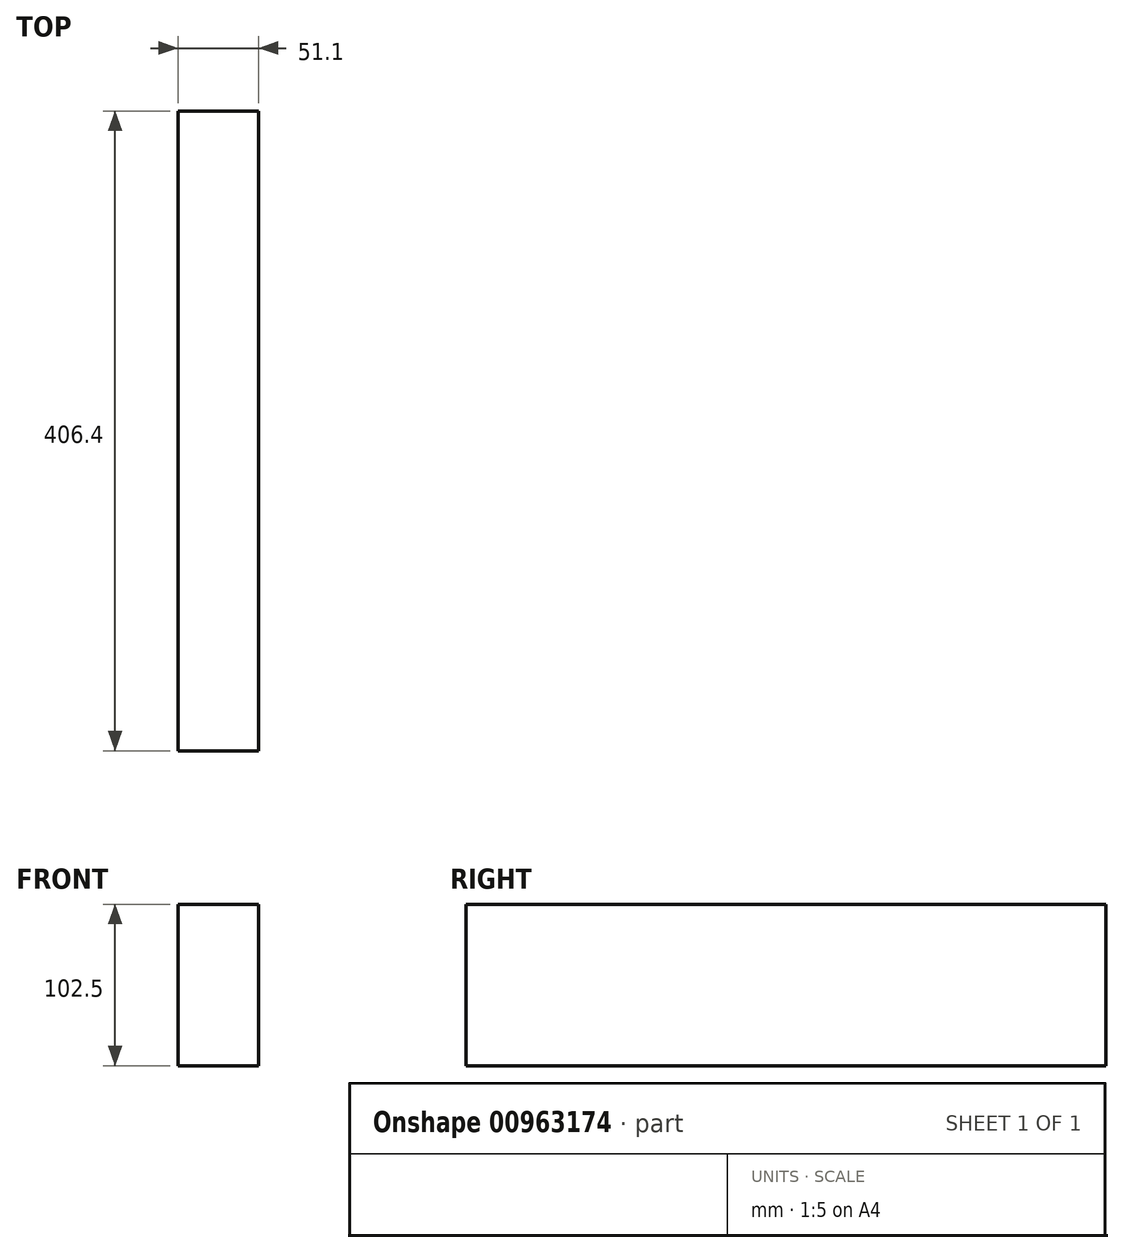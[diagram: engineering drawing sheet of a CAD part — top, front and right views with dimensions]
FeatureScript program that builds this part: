
annotation { "Feature Type Name" : "Feature", "Feature Type Description" : "" }
export const myFeature = defineFeature(function(context is Context, id is Id, definition is map)
    precondition{}
    {
        {
            var Q0;
            Q0=qCreatedBy(makeId("Front.planeOp"),FACE);
            var sketch = newSketch(context, id + "F0", { "sketchPlane" : qUnion([Q0])});
            skLineSegment(sketch, "E0.bottom", {"start": v(-25.55, 51.25) * mm, "end": v(25.55, 51.25) * mm});
            skLineSegment(sketch, "E0.top", {"start": v(-25.55, -51.25) * mm, "end": v(25.55, -51.25) * mm});
            skLineSegment(sketch, "E0.left", {"start": v(-25.55, 51.25) * mm, "end": v(-25.55, -51.25) * mm});
            skLineSegment(sketch, "E0.right", {"start": v(25.55, 51.25) * mm, "end": v(25.55, -51.25) * mm});
            skPoint(sketch, "E0.middle", {"position": v(0, 0) * mm});
            skSolve(sketch);
        }
        {
            var Q0;
            Q0=makeQuery(id+"F0.imprint","IMPRINT",FACE,{"disambiguationData":[TD([[makeQuery(id+"F0.imprint","IMPRINT",EDGE,{"derivedFrom":sQuery(id+"F0.wireOp",EDGE,"E0.bottom")}),-1.0]])]});
            extrude(context, id + "F1", {"entities" : qUnion([Q0]), "depth" : 406.4 * mm, "offsetDistance" : 25.4 * mm});
        }
    });
